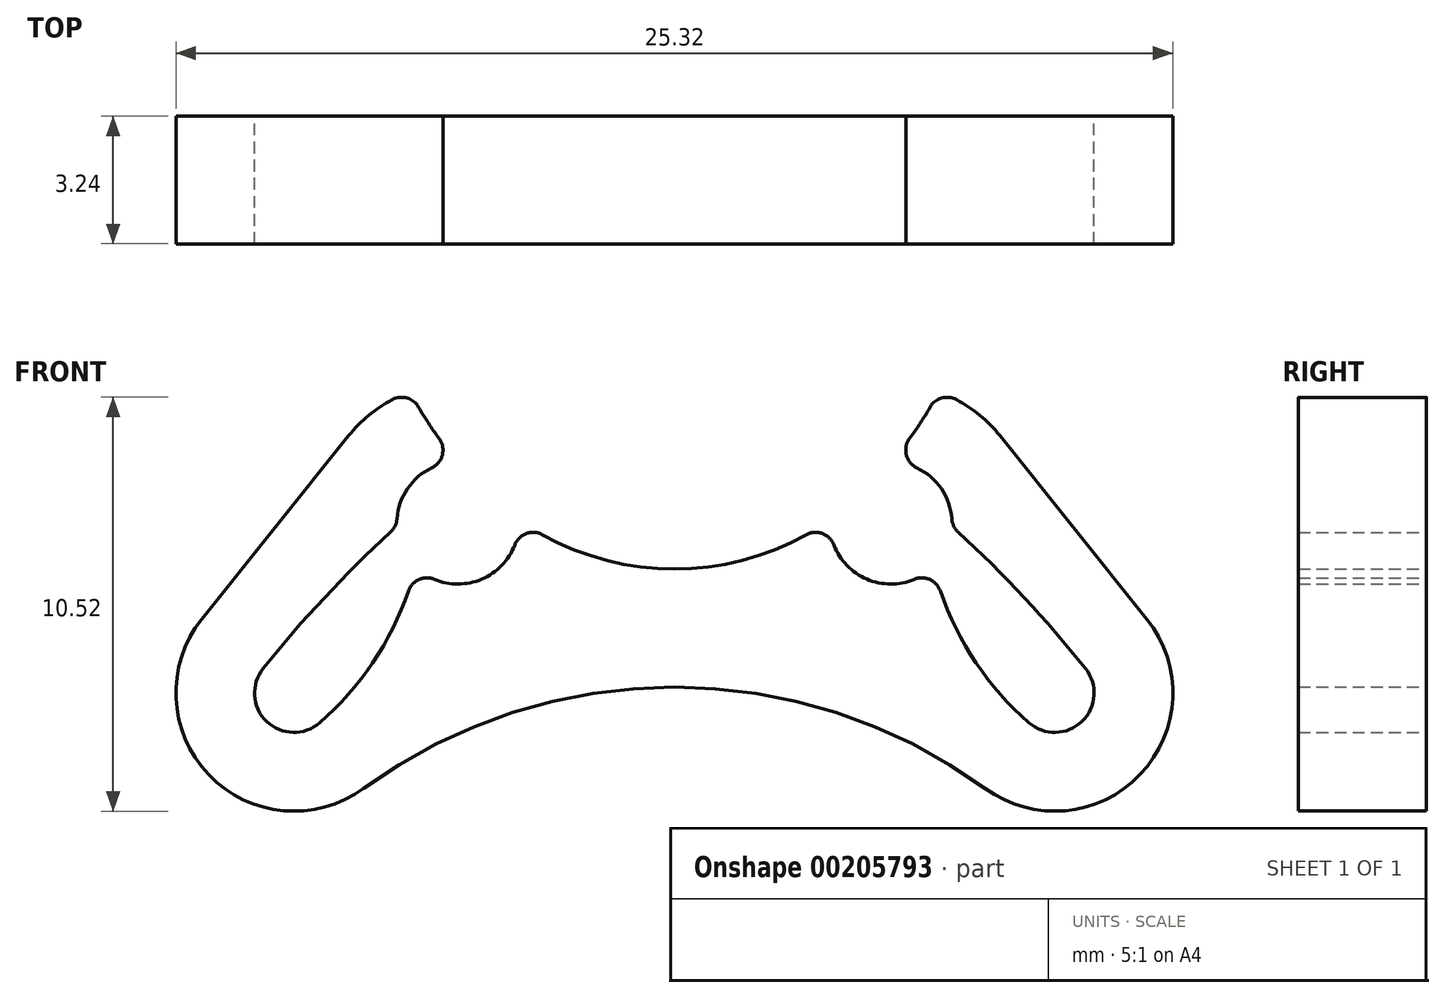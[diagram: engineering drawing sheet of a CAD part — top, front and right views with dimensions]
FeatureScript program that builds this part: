
annotation { "Feature Type Name" : "Feature", "Feature Type Description" : "" }
export const myFeature = defineFeature(function(context is Context, id is Id, definition is map)
    precondition{}
    {
        {
            var Q0;
            Q0=qCreatedBy(makeId("Front.planeOp"),FACE);
            var sketch = newSketch(context, id + "F0", { "sketchPlane" : qUnion([Q0])});
            skCircle(sketch, "E0", {"center": v(0, 0) * mm, "radius": 6.38 * mm});
            skPoint(sketch, "E1", {"position": v(0, 6.38) * mm});
            skPoint(sketch, "E2", {"position": v(0, 11.38) * mm});
            skCircle(sketch, "E3", {"center": v(-5.5, -5.7) * mm, "radius": 1.55 * mm});
            skLineSegment(sketch, "E4", {"start": v(0, 11.38) * mm, "end": v(0, 0) * mm, "construction": true});
            skCircle(sketch, "E5.MirrorC", {"center": v(5.5, -5.7) * mm, "radius": 1.55 * mm});
            skLineSegment(sketch, "E6", {"start": v(-5.5, -5.7) * mm, "end": v(5.5, -5.7) * mm, "construction": true});
            skSolve(sketch);
        }
        {
            var Q0;
            Q0=qCreatedBy(makeId("Front.planeOp"),FACE);
            var sketch = newSketch(context, id + "F1", { "sketchPlane" : qUnion([Q0])});
            skArc(sketch, "E7.0", {"start": v(-3.95, -5.63) * mm, "mid": v(-2.07, -6.56) * mm, "end": v(0, -6.88) * mm});
            skArc(sketch, "E8.3", {"start": v(-6.58, -6.82) * mm, "mid": v(-4.86, -7.12) * mm, "end": v(-3.95, -5.63) * mm});
            skLineSegment(sketch, "E9", {"start": v(0, 0) * mm, "end": v(-9.66, -10.03) * mm, "construction": true});
            skArc(sketch, "E10", {"start": v(-10.44, -9.4) * mm, "mid": v(-10.36, -10.75) * mm, "end": v(-9, -10.78) * mm});
            skLineSegment(sketch, "E11", {"start": v(-5.48, -4.16) * mm, "end": v(-7.05, -5.79) * mm, "construction": true});
            skLineSegment(sketch, "E12", {"start": v(-3.95, -5.63) * mm, "end": v(-5.52, -7.26) * mm, "construction": true});
            skLineSegment(sketch, "E13", {"start": v(-9, -10.78) * mm, "end": v(-4.74, -7.06) * mm, "construction": true});
            skPoint(sketch, "E13.endSnap0", {"position": v(-4.74, -6.44) * mm});
            skLineSegment(sketch, "E14", {"start": v(-6.7, -4.74) * mm, "end": v(-10.44, -9.4) * mm, "construction": true});
            skArc(sketch, "E15.trimOffspring", {"start": v(-12, -8.15) * mm, "mid": v(-11.83, -12.1) * mm, "end": v(-7.9, -12.45) * mm});
            skLineSegment(sketch, "E16", {"start": v(0, 0) * mm, "end": v(0, -9.88) * mm, "construction": true});
            skArc(sketch, "E17", {"start": v(0, -9.88) * mm, "mid": v(-4.15, -10.53) * mm, "end": v(-7.9, -12.45) * mm});
            skLineSegment(sketch, "E18", {"start": v(0, -9.88) * mm, "end": v(-5.5, -9.88) * mm, "construction": true});
            skLineSegment(sketch, "E19", {"start": v(0, -9.88) * mm, "end": v(0, -6.88) * mm});
            skArc(sketch, "E20", {"start": v(-5.48, -4.16) * mm, "mid": v(-6.62, -4.63) * mm, "end": v(-7.05, -5.79) * mm});
            skArc(sketch, "E21", {"start": v(-7.05, -5.79) * mm, "mid": v(-8.82, -7.53) * mm, "end": v(-10.44, -9.4) * mm});
            skLineSegment(sketch, "E22", {"start": v(-12, -8.15) * mm, "end": v(-8.27, -3.49) * mm});
            skArc(sketch, "E23", {"start": v(-6.7, -2.37) * mm, "mid": v(-6.16, -3.3) * mm, "end": v(-5.48, -4.16) * mm});
            skArc(sketch, "E24", {"start": v(-9, -10.78) * mm, "mid": v(-7.49, -8.99) * mm, "end": v(-6.58, -6.82) * mm});
            skLineSegment(sketch, "E25", {"start": v(-9.66, -13.03) * mm, "end": v(0, -13.03) * mm, "construction": true});
            skLineSegment(sketch, "E26", {"start": v(0, -13.03) * mm, "end": v(0, -6.88) * mm, "construction": true});
            skArc(sketch, "E27.trimOffspring", {"start": v(-6.7, -2.37) * mm, "mid": v(-7.56, -2.82) * mm, "end": v(-8.27, -3.49) * mm});
            skPoint(sketch, "E28.orphan", {"position": v(0, 8.37) * mm});
            skSolve(sketch);
        }
        {
            var Q0;
            Q0=qSketchRegion(id+"F1",true);
            extrude(context, id + "F2", {"entities" : qUnion([Q0]), "depth" : 3.25 * mm, "symmetric" : true});
        }
        {
            var Q0;
            Q0=makeQuery(id+"F2.opExtrude","SWEPT_EDGE",EDGE,{"disambiguationData":[OSD([sQuery(id+"F1.wireOp",EDGE,"E8.3"),sQuery(id+"F1.wireOp",EDGE,"f16a48b5-7a2a-4cbf-833e-9f4b7a7ec827.trimOffspring")])]});
            var Q1;
            Q1=makeQuery(id+"F2.opExtrude","SWEPT_EDGE",EDGE,{"disambiguationData":[OSD([sQuery(id+"F1.wireOp",EDGE,"0503ed2f-4905-41a0-8b90-6c5d83e06de4"),sQuery(id+"F1.wireOp",EDGE,"E8.3")])]});
            var Q2;
            Q2=makeQuery(id+"F2.opExtrude","SWEPT_EDGE",EDGE,{"disambiguationData":[OSD([sQuery(id+"F1.wireOp",EDGE,"E7.0"),sQuery(id+"F1.wireOp",EDGE,"E8.3")])]});
            var Q3;
            Q3=makeQuery(id+"F2.opExtrude","SWEPT_EDGE",EDGE,{"disambiguationData":[OSD([sQuery(id+"F1.wireOp",EDGE,"E20"),sQuery(id+"F1.wireOp",EDGE,"E21")])]});
            var Q4;
            Q4=makeQuery(id+"F2.opExtrude","SWEPT_EDGE",EDGE,{"disambiguationData":[OSD([sQuery(id+"F1.wireOp",EDGE,"E20"),sQuery(id+"F1.wireOp",EDGE,"aa0188ab-c223-4f96-b803-20454a8c8853")])]});
            var Q5;
            Q5=makeQuery(id+"F2.opExtrude","SWEPT_EDGE",EDGE,{"disambiguationData":[OSD([sQuery(id+"F1.wireOp",EDGE,"e83e305f-1027-4866-97f5-19716599f6f7"),sQuery(id+"F1.wireOp",EDGE,"E8.3")])]});
            var Q6;
            Q6=makeQuery(id+"F2.opExtrude","SWEPT_EDGE",EDGE,{"disambiguationData":[OSD([sQuery(id+"F1.wireOp",EDGE,"E10"),sQuery(id+"F1.wireOp",EDGE,"e83e305f-1027-4866-97f5-19716599f6f7")])]});
            var Q7;
            Q7=makeQuery(id+"F2.opExtrude","SWEPT_EDGE",EDGE,{"disambiguationData":[OSD([sQuery(id+"F1.wireOp",EDGE,"E23"),sQuery(id+"F1.wireOp",EDGE,"E27.trimOffspring")])]});
            fillet(context, id + "F3", {"entities" : qUnion([Q0, Q1, Q2, Q3, Q4, Q5, Q6, Q7]), "radius" : 0.5 * mm, "tangentPropagation" : true, "allowEdgeOverflow" : false});
        }
        {
            var Q0;
            Q0=makeQuery(id+"F2.opExtrude","SWEPT_BODY",BODY,{"disambiguationData":[OSD([sQuery(id+"F1.wireOp",EDGE,"91029bab-c422-4aac-b43c-f8eb8f7441cb.0"),sQuery(id+"F1.wireOp",EDGE,"E7.0"),sQuery(id+"F1.wireOp",EDGE,"E8.0"),sQuery(id+"F1.wireOp",EDGE,"E8.3"),sQuery(id+"F1.wireOp",EDGE,"4fe737ca-cd33-4ae7-bfb5-aca6cdd2fbdd"),sQuery(id+"F1.wireOp",EDGE,"E10"),sQuery(id+"F1.wireOp",EDGE,"87521696-a49b-46d6-ae6d-b95a5258b794"),sQuery(id+"F1.wireOp",EDGE,"3ad451f8-88f0-40d6-b978-8860d0f46c41"),sQuery(id+"F1.wireOp",EDGE,"RmzYGLSE-aIne-cmcq-fouj-xsO9WjanKBXf"),sQuery(id+"F1.wireOp",EDGE,"E1ndacnS-k5oY-T1jz-uEtG-vA6wWoizQWTL"),sQuery(id+"F1.wireOp",EDGE,"290a5299-caae-4b93-a680-34ceb27d99b0"),sQuery(id+"F1.wireOp",EDGE,"acf9eb55-ab42-4665-aab6-df971979b8c6"),sQuery(id+"F1.wireOp",EDGE,"0503ed2f-4905-41a0-8b90-6c5d83e06de4"),sQuery(id+"F1.wireOp",EDGE,"e83e305f-1027-4866-97f5-19716599f6f7"),sQuery(id+"F1.wireOp",EDGE,"E8.3"),sQuery(id+"F1.wireOp",EDGE,"E15.trimOffspring"),sQuery(id+"F1.wireOp",EDGE,"140a15c2-b3ae-4d8c-875c-2f7ce67bd9a0.trimOffspring"),sQuery(id+"F1.wireOp",EDGE,"f16a48b5-7a2a-4cbf-833e-9f4b7a7ec827.trimOffspring"),sQuery(id+"F1.wireOp",EDGE,"c726c67e-1b0a-4414-994c-10f8da0a7d9b.trimOffspring"),sQuery(id+"F1.wireOp",EDGE,"E17"),sQuery(id+"F1.wireOp",EDGE,"9d4cf9fb-cccf-4056-9c7a-a0118e21bfc9.trimOffspring"),sQuery(id+"F1.wireOp",EDGE,"aw0qZEzT-GYTq-v6Y8-Owwz-bXgHvjQE39bA"),sQuery(id+"F1.wireOp",EDGE,"E19"),sQuery(id+"F1.wireOp",EDGE,"e7ad43b5-d072-4a5a-872d-9ebe676b2ed9.trimOffspring")])]});
            var Q1;
            Q1=qCreatedBy(makeId("Right.planeOp"),FACE);
            mirror(context, id + "F4", {"operationType" : NewBodyOperationType.ADD, "entities" : qUnion([Q0]), "mirrorPlane" : qUnion([Q1])});
        }
    });
